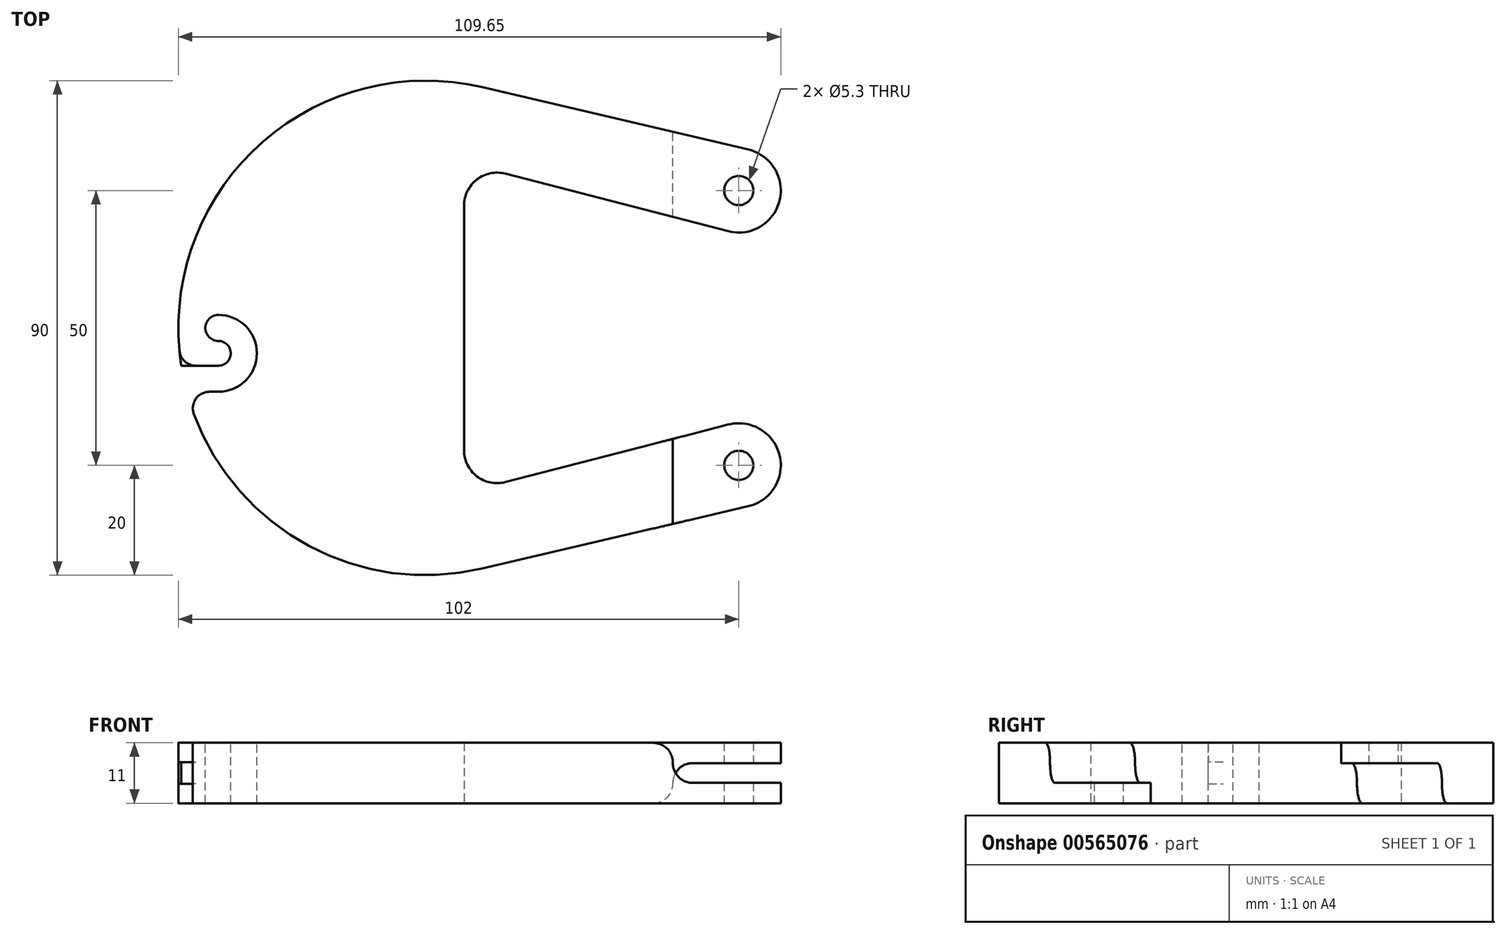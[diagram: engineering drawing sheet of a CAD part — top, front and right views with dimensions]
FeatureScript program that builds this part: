
annotation { "Feature Type Name" : "Feature", "Feature Type Description" : "" }
export const myFeature = defineFeature(function(context is Context, id is Id, definition is map)
    precondition{}
    {
        {
            var Q0;
            Q0=qCreatedBy(makeId("Top.planeOp"),FACE);
            var sketch = newSketch(context, id + "F0", { "sketchPlane" : qUnion([Q0])});
            skLineSegment(sketch, "E0", {"start": v(0, -25) * mm, "end": v(98, -25) * mm, "construction": true});
            skCircle(sketch, "E1", {"center": v(98, -25) * mm, "radius": 2.65 * mm});
            skLineSegment(sketch, "E2", {"start": v(0, 25) * mm, "end": v(98, 25) * mm, "construction": true});
            skLineSegment(sketch, "E3", {"start": v(0, 25) * mm, "end": v(0, 0) * mm, "construction": true});
            skLineSegment(sketch, "E4", {"start": v(0, 0) * mm, "end": v(0, -25) * mm, "construction": true});
            skCircle(sketch, "E5", {"center": v(98, 25) * mm, "radius": 2.65 * mm});
            skCircle(sketch, "E6.0", {"center": v(98, -25) * mm, "radius": 7.65 * mm});
            skLineSegment(sketch, "E7", {"start": v(51.27, -43.81) * mm, "end": v(99.75, -32.45) * mm});
            skCircle(sketch, "E8", {"center": v(98, 25) * mm, "radius": 7.65 * mm});
            skLineSegment(sketch, "E9", {"start": v(99.75, 32.45) * mm, "end": v(51.27, 43.81) * mm});
            skLineSegment(sketch, "E10", {"start": v(48, 22.26) * mm, "end": v(48, -22.26) * mm});
            skLineSegment(sketch, "E11", {"start": v(0, 0) * mm, "end": v(48, 0) * mm, "construction": true});
            skLineSegment(sketch, "E12", {"start": v(55.5, -28.07) * mm, "end": v(96.09, -17.6) * mm});
            skLineSegment(sketch, "E13", {"start": v(96.09, 17.6) * mm, "end": v(55.5, 28.07) * mm});
            skPoint(sketch, "E14.visualSharp", {"position": v(48, 30) * mm});
            skArc(sketch, "E14.filletArc", {"start": v(55.5, 28.07) * mm, "mid": v(50.33, 27) * mm, "end": v(48, 22.26) * mm});
            skPoint(sketch, "E15.visualSharp", {"position": v(48, -30) * mm});
            skArc(sketch, "E15.filletArc", {"start": v(48, -22.26) * mm, "mid": v(50.33, -27) * mm, "end": v(55.5, -28.07) * mm});
            skArc(sketch, "E16", {"start": v(51.27, 43.81) * mm, "mid": v(-4, 0) * mm, "end": v(51.27, -43.81) * mm});
            skSolve(sketch);
        }
        {
            var Q0;
            {var subQ3=sQuery(id+"F0.wireOp",EDGE,"E7");Q0=makeQuery(id+"F0.imprint","IMPRINT",FACE,{"disambiguationData":[TD([[makeQuery(id+"F0.imprint","IMPRINT",EDGE,{"derivedFrom":subQ3}),1.0]])]});}
            var Q1;
            Q1=makeQuery(id+"F0.imprint","IMPRINT",FACE,{"disambiguationData":[TD([[makeQuery(id+"F0.imprint","IMPRINT",EDGE,{"derivedFrom":sQuery(id+"F0.wireOp",EDGE,"E5")}),-1.0]])]});
            var Q2;
            Q2=makeQuery(id+"F0.imprint","IMPRINT",FACE,{"disambiguationData":[TD([[makeQuery(id+"F0.imprint","IMPRINT",EDGE,{"derivedFrom":sQuery(id+"F0.wireOp",EDGE,"E1")}),-1.0]])]});
            extrude(context, id + "F1", {"entities" : qUnion([Q0, Q1, Q2]), "depth" : 4 * mm, "offsetDistance" : 25 * mm});
        }
        {
            var Q0;
            Q0=makeQuery(id+"F1.opExtrude","CAP_FACE",FACE,{"disambiguationData":[OSD([sQuery(id+"F0.wireOp",EDGE,"xxKo6WRD-6QPB-TjOC-Ujmc-5RzxxUmcmt8J"),sQuery(id+"F0.wireOp",EDGE,"E1"),sQuery(id+"F0.wireOp",EDGE,"E5"),sQuery(id+"F0.wireOp",EDGE,"E6.0"),sQuery(id+"F0.wireOp",EDGE,"E7"),sQuery(id+"F0.wireOp",EDGE,"E8"),sQuery(id+"F0.wireOp",EDGE,"E9"),sQuery(id+"F0.wireOp",EDGE,"E10"),sQuery(id+"F0.wireOp",EDGE,"E12"),sQuery(id+"F0.wireOp",EDGE,"E13"),sQuery(id+"F0.wireOp",EDGE,"E14.filletArc"),sQuery(id+"F0.wireOp",EDGE,"E15.filletArc")])],"isStart":false});
            var sketch = newSketch(context, id + "F2", { "sketchPlane" : qUnion([Q0])});
            skArc(sketch, "E17", {"start": v(3.28, -11.63) * mm, "mid": v(10.28, -4.63) * mm, "end": v(3.28, 2.37) * mm});
            skPoint(sketch, "E17.centerSnap0", {"position": v(-4, 0) * mm});
            skArc(sketch, "E18", {"start": v(3.28, -6.88) * mm, "mid": v(5.53, -4.63) * mm, "end": v(3.28, -2.38) * mm});
            skArc(sketch, "E19", {"start": v(3.28, 2.37) * mm, "mid": v(0.9, 0) * mm, "end": v(3.28, -2.38) * mm});
            skLineSegment(sketch, "E20", {"start": v(3.28, -6.88) * mm, "end": v(-3.47, -6.88) * mm});
            skLineSegment(sketch, "E21", {"start": v(3.28, -11.63) * mm, "end": v(-2.47, -11.63) * mm});
            skLineSegment(sketch, "E22.0.0", {"start": v(99.75, -32.45) * mm, "end": v(51.27, -43.81) * mm});
            skArc(sketch, "E22.0.1", {"start": v(51.27, -43.81) * mm, "mid": v(-4, 0) * mm, "end": v(51.27, 43.81) * mm});
            skLineSegment(sketch, "E22.0.2", {"start": v(51.27, 43.81) * mm, "end": v(99.75, 32.45) * mm});
            skArc(sketch, "E22.0.3", {"start": v(99.75, 32.45) * mm, "mid": v(105.43, 23.17) * mm, "end": v(96.09, 17.6) * mm});
            skLineSegment(sketch, "E22.0.4", {"start": v(96.09, 17.6) * mm, "end": v(55.5, 28.07) * mm});
            skArc(sketch, "E22.0.5", {"start": v(55.5, 28.07) * mm, "mid": v(50.33, 27) * mm, "end": v(48, 22.26) * mm});
            skLineSegment(sketch, "E22.0.6", {"start": v(48, 22.26) * mm, "end": v(48, -22.26) * mm});
            skArc(sketch, "E22.0.7", {"start": v(48, -22.26) * mm, "mid": v(50.33, -27) * mm, "end": v(55.5, -28.07) * mm});
            skLineSegment(sketch, "E22.0.8", {"start": v(55.5, -28.07) * mm, "end": v(96.09, -17.6) * mm});
            skArc(sketch, "E22.0.9", {"start": v(96.09, -17.6) * mm, "mid": v(105.43, -23.17) * mm, "end": v(99.75, -32.45) * mm});
            skSolve(sketch);
        }
        {
            var Q0;
            Q0=makeQuery(id+"F2.imprint","IMPRINT",FACE,{"disambiguationData":[TD([[makeQuery(id+"F2.imprint","IMPRINT",EDGE,{"derivedFrom":sQuery(id+"F2.wireOp",EDGE,"E17")}),1.0]])]});
            extrude(context, id + "F3", {"entities" : qUnion([Q0]), "operationType" : NewBodyOperationType.REMOVE, "endBound" : BoundingType.THROUGH_ALL, "oppositeDirection" : true, "depth" : 25 * mm, "offsetDistance" : 25 * mm});
        }
        {
            var Q0;
            Q0=makeQuery(id+"F3.boolean.opBoolean","COPY",EDGE,{"derivedFrom":makeQuery(id+"F3.opExtrude","SWEPT_EDGE",EDGE,{"disambiguationData":[OSD([sQuery(id+"F0.wireOp",EDGE,"xxKo6WRD-6QPB-TjOC-Ujmc-5RzxxUmcmt8J"),sQuery(id+"F2.wireOp",EDGE,"E20")])]})});
            var Q1;
            Q1=makeQuery(id+"F3.boolean.opBoolean","COPY",EDGE,{"derivedFrom":makeQuery(id+"F3.opExtrude","SWEPT_EDGE",EDGE,{"disambiguationData":[OSD([sQuery(id+"F0.wireOp",EDGE,"xxKo6WRD-6QPB-TjOC-Ujmc-5RzxxUmcmt8J"),sQuery(id+"F2.wireOp",EDGE,"E21")])]})});
            fillet(context, id + "F4", {"entities" : qUnion([Q0, Q1]), "radius" : 3 * mm, "tangentPropagation" : true, "allowEdgeOverflow" : false});
        }
        {
            var Q0;
            Q0=makeQuery(id+"F1.opExtrude","CAP_FACE",FACE,{"disambiguationData":[OSD([sQuery(id+"F0.wireOp",EDGE,"xxKo6WRD-6QPB-TjOC-Ujmc-5RzxxUmcmt8J"),sQuery(id+"F0.wireOp",EDGE,"E1"),sQuery(id+"F0.wireOp",EDGE,"E5"),sQuery(id+"F0.wireOp",EDGE,"E6.0"),sQuery(id+"F0.wireOp",EDGE,"E7"),sQuery(id+"F0.wireOp",EDGE,"E8"),sQuery(id+"F0.wireOp",EDGE,"E9"),sQuery(id+"F0.wireOp",EDGE,"E10"),sQuery(id+"F0.wireOp",EDGE,"E12"),sQuery(id+"F0.wireOp",EDGE,"E13"),sQuery(id+"F0.wireOp",EDGE,"E14.filletArc"),sQuery(id+"F0.wireOp",EDGE,"E15.filletArc")])],"isStart":true});
            var sketch = newSketch(context, id + "F5", { "sketchPlane" : qUnion([Q0])});
            skArc(sketch, "E23.0.4", {"start": v(99.75, -32.45) * mm, "mid": v(105.43, -23.17) * mm, "end": v(96.09, -17.6) * mm});
            skLineSegment(sketch, "E23.0.5", {"start": v(96.09, -17.6) * mm, "end": v(55.5, -28.07) * mm});
            skArc(sketch, "E23.0.6", {"start": v(55.5, -28.07) * mm, "mid": v(50.33, -27) * mm, "end": v(48, -22.26) * mm});
            skLineSegment(sketch, "E23.0.7", {"start": v(48, -22.26) * mm, "end": v(48, 22.26) * mm});
            skLineSegment(sketch, "E23.0.9", {"start": v(55.5, 28.07) * mm, "end": v(96.09, 17.6) * mm});
            skArc(sketch, "E23.0.10", {"start": v(96.09, 17.6) * mm, "mid": v(105.43, 23.17) * mm, "end": v(99.75, 32.45) * mm});
            skLineSegment(sketch, "E23.0.11", {"start": v(99.75, 32.45) * mm, "end": v(51.27, 43.81) * mm});
            skCircle(sketch, "E24.0", {"center": v(98, 25) * mm, "radius": 2.65 * mm});
            skLineSegment(sketch, "E25", {"start": v(82, 36.6) * mm, "end": v(82, 21.23) * mm});
            skSolve(sketch);
        }
        {
            var Q0;
            {var subQ1=sQuery(id+"F5.wireOp",EDGE,"E23.0.10");Q0=makeQuery(id+"F5.imprint","IMPRINT",FACE,{"disambiguationData":[TD([[makeQuery(id+"F5.imprint","IMPRINT",EDGE,{"derivedFrom":subQ1}),-1.0]])]});}
            extrude(context, id + "F6", {"entities" : qUnion([Q0]), "operationType" : NewBodyOperationType.ADD, "depth" : 3.5 * mm, "offsetDistance" : 25 * mm});
        }
        {
            var Q0;
            Q0=makeQuery(id+"F1.opExtrude","CAP_FACE",FACE,{"disambiguationData":[OSD([sQuery(id+"F0.wireOp",EDGE,"xxKo6WRD-6QPB-TjOC-Ujmc-5RzxxUmcmt8J"),sQuery(id+"F0.wireOp",EDGE,"E1"),sQuery(id+"F0.wireOp",EDGE,"E5"),sQuery(id+"F0.wireOp",EDGE,"E6.0"),sQuery(id+"F0.wireOp",EDGE,"E7"),sQuery(id+"F0.wireOp",EDGE,"E8"),sQuery(id+"F0.wireOp",EDGE,"E9"),sQuery(id+"F0.wireOp",EDGE,"E10"),sQuery(id+"F0.wireOp",EDGE,"E12"),sQuery(id+"F0.wireOp",EDGE,"E13"),sQuery(id+"F0.wireOp",EDGE,"E14.filletArc"),sQuery(id+"F0.wireOp",EDGE,"E15.filletArc")])],"isStart":false});
            var sketch = newSketch(context, id + "F7", { "sketchPlane" : qUnion([Q0])});
            skLineSegment(sketch, "E26", {"start": v(86, -20.2) * mm, "end": v(86, -35.67) * mm});
            skArc(sketch, "E27.0.10", {"start": v(99.75, -32.45) * mm, "mid": v(105.43, -23.17) * mm, "end": v(96.09, -17.6) * mm});
            skLineSegment(sketch, "E27.0.11", {"start": v(96.09, -17.6) * mm, "end": v(55.5, -28.07) * mm});
            skArc(sketch, "E27.0.12", {"start": v(55.5, -28.07) * mm, "mid": v(50.33, -27) * mm, "end": v(48, -22.26) * mm});
            skLineSegment(sketch, "E27.0.13", {"start": v(48, -22.26) * mm, "end": v(48, 22.26) * mm});
            skArc(sketch, "E27.0.14", {"start": v(48, 22.26) * mm, "mid": v(50.33, 27) * mm, "end": v(55.5, 28.07) * mm});
            skLineSegment(sketch, "E27.0.15", {"start": v(55.5, 28.07) * mm, "end": v(96.09, 17.6) * mm});
            skArc(sketch, "E27.0.16", {"start": v(96.09, 17.6) * mm, "mid": v(105.43, 23.17) * mm, "end": v(99.75, 32.45) * mm});
            skCircle(sketch, "E28.0", {"center": v(98, -25) * mm, "radius": 2.65 * mm});
            skSolve(sketch);
        }
        {
            var Q0;
            {var subQ2=sQuery(id+"F7.wireOp",EDGE,"E26");Q0=makeQuery(id+"F7.imprint","IMPRINT",FACE,{"disambiguationData":[TD([[makeQuery(id+"F7.imprint","IMPRINT",EDGE,{"derivedFrom":subQ2}),1.0]])]});}
            extrude(context, id + "F8", {"entities" : qUnion([Q0]), "operationType" : NewBodyOperationType.REMOVE, "oppositeDirection" : true, "depth" : 3.8 * mm, "offsetDistance" : 25 * mm});
        }
        {
            var Q0;
            Q0=qCreatedBy(makeId("Front.planeOp"),FACE);
            var sketch = newSketch(context, id + "F9", { "sketchPlane" : qUnion([Q0])});
            skLineSegment(sketch, "E29.0", {"start": v(82, -3.5) * mm, "end": v(82, 0) * mm});
            skLineSegment(sketch, "E30.0", {"start": v(86, 0.2) * mm, "end": v(86, 4) * mm});
            skLineSegment(sketch, "E31.0", {"start": v(55.5, 0) * mm, "end": v(82, 0) * mm});
            skLineSegment(sketch, "E32.0", {"start": v(82, -3.5) * mm, "end": v(96.09, -3.5) * mm});
            skLineSegment(sketch, "E33", {"start": v(82, -3.5) * mm, "end": v(55.5, 0) * mm});
            skSolve(sketch);
        }
        {
            var Q0;
            Q0=makeQuery(id+"F1.opExtrude","CAP_FACE",FACE,{"disambiguationData":[OSD([sQuery(id+"F0.wireOp",EDGE,"xxKo6WRD-6QPB-TjOC-Ujmc-5RzxxUmcmt8J"),sQuery(id+"F0.wireOp",EDGE,"E1"),sQuery(id+"F0.wireOp",EDGE,"E5"),sQuery(id+"F0.wireOp",EDGE,"E6.0"),sQuery(id+"F0.wireOp",EDGE,"E7"),sQuery(id+"F0.wireOp",EDGE,"E8"),sQuery(id+"F0.wireOp",EDGE,"E9"),sQuery(id+"F0.wireOp",EDGE,"E10"),sQuery(id+"F0.wireOp",EDGE,"E12"),sQuery(id+"F0.wireOp",EDGE,"E13"),sQuery(id+"F0.wireOp",EDGE,"E14.filletArc"),sQuery(id+"F0.wireOp",EDGE,"E15.filletArc")])],"isStart":false});
            var sketch = newSketch(context, id + "F10", { "sketchPlane" : qUnion([Q0])});
            skArc(sketch, "E34.0.2", {"start": v(55.5, -28.07) * mm, "mid": v(50.33, -27) * mm, "end": v(48, -22.26) * mm});
            skLineSegment(sketch, "E34.0.3", {"start": v(48, -22.26) * mm, "end": v(48, 22.26) * mm});
            skArc(sketch, "E34.0.4", {"start": v(48, 22.26) * mm, "mid": v(50.33, 27) * mm, "end": v(55.5, 28.07) * mm});
            skLineSegment(sketch, "E34.0.5", {"start": v(55.5, 28.07) * mm, "end": v(96.09, 17.6) * mm});
            skArc(sketch, "E34.0.6", {"start": v(96.09, 17.6) * mm, "mid": v(105.43, 23.17) * mm, "end": v(99.75, 32.45) * mm});
            skLineSegment(sketch, "E34.0.7", {"start": v(99.75, 32.45) * mm, "end": v(99.75, 32.45) * mm});
            skLineSegment(sketch, "E34.0.14", {"start": v(3.28, -11.63) * mm, "end": v(1.63, -11.63) * mm});
            skCircle(sketch, "E35.0", {"center": v(98, 25) * mm, "radius": 2.65 * mm});
            skLineSegment(sketch, "E36", {"start": v(82, 21.23) * mm, "end": v(82, 36.6) * mm});
            skLineSegment(sketch, "E37.0.7", {"start": v(99.75, 32.45) * mm, "end": v(51.27, 43.81) * mm});
            skArc(sketch, "E37.0.16", {"start": v(-1.18, -15.67) * mm, "mid": v(19.73, -39.65) * mm, "end": v(51.27, -43.81) * mm});
            skArc(sketch, "E38.0.8", {"start": v(51.27, 43.81) * mm, "mid": v(11.45, 33.94) * mm, "end": v(-3.8, -4.15) * mm});
            skArc(sketch, "E38.0.9", {"start": v(-3.8, -4.15) * mm, "mid": v(-2.84, -6.1) * mm, "end": v(-0.82, -6.88) * mm});
            skLineSegment(sketch, "E38.0.10", {"start": v(-0.82, -6.88) * mm, "end": v(3.28, -6.88) * mm});
            skArc(sketch, "E38.0.11", {"start": v(3.28, -6.88) * mm, "mid": v(5.53, -4.63) * mm, "end": v(3.28, -2.38) * mm});
            skArc(sketch, "E38.0.12", {"start": v(3.28, -2.38) * mm, "mid": v(0.9, 0) * mm, "end": v(3.28, 2.37) * mm});
            skArc(sketch, "E38.0.13", {"start": v(3.28, 2.37) * mm, "mid": v(10.28, -4.63) * mm, "end": v(3.28, -11.63) * mm});
            skArc(sketch, "E38.0.15", {"start": v(1.63, -11.63) * mm, "mid": v(-0.83, -12.91) * mm, "end": v(-1.18, -15.67) * mm});
            skSolve(sketch);
        }
        {
            var Q0;
            Q0=makeQuery(id+"F10.imprint","IMPRINT",FACE,{"disambiguationData":[TD([[makeQuery(id+"F10.imprint","IMPRINT",EDGE,{"derivedFrom":sQuery(id+"F10.wireOp",EDGE,"E35.0")}),-1.0]])]});
            extrude(context, id + "F11", {"entities" : qUnion([Q0]), "operationType" : NewBodyOperationType.ADD, "depth" : 3.5 * mm, "offsetDistance" : 25 * mm});
        }
        {
            var Q0;
            Q0=makeQuery(id+"F1.opExtrude","CAP_FACE",FACE,{"disambiguationData":[OSD([sQuery(id+"F0.wireOp",EDGE,"xxKo6WRD-6QPB-TjOC-Ujmc-5RzxxUmcmt8J"),sQuery(id+"F0.wireOp",EDGE,"E1"),sQuery(id+"F0.wireOp",EDGE,"E5"),sQuery(id+"F0.wireOp",EDGE,"E6.0"),sQuery(id+"F0.wireOp",EDGE,"E7"),sQuery(id+"F0.wireOp",EDGE,"E8"),sQuery(id+"F0.wireOp",EDGE,"E9"),sQuery(id+"F0.wireOp",EDGE,"E10"),sQuery(id+"F0.wireOp",EDGE,"E12"),sQuery(id+"F0.wireOp",EDGE,"E13"),sQuery(id+"F0.wireOp",EDGE,"E14.filletArc"),sQuery(id+"F0.wireOp",EDGE,"E15.filletArc")])],"isStart":true});
            var sketch = newSketch(context, id + "F12", { "sketchPlane" : qUnion([Q0])});
            skLineSegment(sketch, "E39", {"start": v(86, -20.2) * mm, "end": v(86, -35.67) * mm});
            skLineSegment(sketch, "E40.0.0", {"start": v(55.5, 28.07) * mm, "end": v(55.5, 42.82) * mm});
            skLineSegment(sketch, "E40.0.1", {"start": v(55.5, 42.82) * mm, "end": v(51.27, 43.81) * mm});
            skArc(sketch, "E40.0.12", {"start": v(99.75, -32.45) * mm, "mid": v(105.43, -23.17) * mm, "end": v(96.09, -17.6) * mm});
            skLineSegment(sketch, "E40.0.13", {"start": v(96.09, -17.6) * mm, "end": v(55.5, -28.07) * mm});
            skArc(sketch, "E40.0.14", {"start": v(55.5, -28.07) * mm, "mid": v(50.33, -27) * mm, "end": v(48, -22.26) * mm});
            skLineSegment(sketch, "E40.0.15", {"start": v(48, -22.26) * mm, "end": v(48, 22.26) * mm});
            skArc(sketch, "E40.0.16", {"start": v(48, 22.26) * mm, "mid": v(50.33, 27) * mm, "end": v(55.5, 28.07) * mm});
            skCircle(sketch, "E41.0", {"center": v(98, -25) * mm, "radius": 2.65 * mm});
            skArc(sketch, "E42.0.2", {"start": v(51.27, 43.81) * mm, "mid": v(19.73, 39.65) * mm, "end": v(-1.18, 15.67) * mm});
            skArc(sketch, "E42.0.3", {"start": v(-1.18, 15.67) * mm, "mid": v(-0.83, 12.91) * mm, "end": v(1.63, 11.63) * mm});
            skLineSegment(sketch, "E42.0.4", {"start": v(1.63, 11.63) * mm, "end": v(3.28, 11.63) * mm});
            skArc(sketch, "E42.0.5", {"start": v(3.28, 11.63) * mm, "mid": v(10.28, 4.63) * mm, "end": v(3.28, -2.37) * mm});
            skArc(sketch, "E42.0.6", {"start": v(3.28, -2.37) * mm, "mid": v(0.9, 0) * mm, "end": v(3.28, 2.38) * mm});
            skArc(sketch, "E42.0.7", {"start": v(3.28, 2.38) * mm, "mid": v(5.53, 4.63) * mm, "end": v(3.28, 6.88) * mm});
            skLineSegment(sketch, "E42.0.8", {"start": v(3.28, 6.88) * mm, "end": v(-0.82, 6.88) * mm});
            skArc(sketch, "E42.0.9", {"start": v(-0.82, 6.88) * mm, "mid": v(-2.84, 6.1) * mm, "end": v(-3.8, 4.15) * mm});
            skArc(sketch, "E42.0.10", {"start": v(-3.8, 4.15) * mm, "mid": v(11.45, -33.94) * mm, "end": v(51.27, -43.81) * mm});
            skLineSegment(sketch, "E42.0.11", {"start": v(51.27, -43.81) * mm, "end": v(99.75, -32.45) * mm});
            skSolve(sketch);
        }
        {
            var Q0;
            {var subQ2=sQuery(id+"F12.wireOp",EDGE,"E39");Q0=makeQuery(id+"F12.imprint","IMPRINT",FACE,{"disambiguationData":[TD([[makeQuery(id+"F12.imprint","IMPRINT",EDGE,{"derivedFrom":subQ2}),1.0]])]});}
            extrude(context, id + "F13", {"entities" : qUnion([Q0]), "operationType" : NewBodyOperationType.REMOVE, "oppositeDirection" : true, "depth" : 3.8 * mm, "offsetDistance" : 25 * mm});
        }
        {
            var Q0;
            Q0=qCreatedBy(makeId("Front.planeOp"),FACE);
            var sketch = newSketch(context, id + "F14", { "sketchPlane" : qUnion([Q0])});
            skLineSegment(sketch, "E43.0", {"start": v(82, 4) * mm, "end": v(82, 7.5) * mm});
            skLineSegment(sketch, "E44.0", {"start": v(82, 4) * mm, "end": v(51.27, 4) * mm});
            skLineSegment(sketch, "E45.0", {"start": v(82, 4) * mm, "end": v(55.5, 4) * mm});
            skLineSegment(sketch, "E46", {"start": v(82, 7.5) * mm, "end": v(55.5, 4) * mm});
            skSolve(sketch);
        }
        {
            var Q0;
            Q0=makeQuery(id+"F1.opExtrude","CAP_FACE",FACE,{"disambiguationData":[OSD([sQuery(id+"F0.wireOp",EDGE,"E1"),sQuery(id+"F0.wireOp",EDGE,"E5"),sQuery(id+"F0.wireOp",EDGE,"E6.0"),sQuery(id+"F0.wireOp",EDGE,"E7"),sQuery(id+"F0.wireOp",EDGE,"E8"),sQuery(id+"F0.wireOp",EDGE,"E9"),sQuery(id+"F0.wireOp",EDGE,"E10"),sQuery(id+"F0.wireOp",EDGE,"E12"),sQuery(id+"F0.wireOp",EDGE,"E13"),sQuery(id+"F0.wireOp",EDGE,"E14.filletArc"),sQuery(id+"F0.wireOp",EDGE,"E15.filletArc"),sQuery(id+"F0.wireOp",EDGE,"E16")])],"isStart":false});
            var sketch = newSketch(context, id + "F15", { "sketchPlane" : qUnion([Q0])});
            skLineSegment(sketch, "E47.0.0", {"start": v(55.5, 28.07) * mm, "end": v(82, 21.23) * mm});
            skLineSegment(sketch, "E47.0.1", {"start": v(82, 21.23) * mm, "end": v(82, 36.6) * mm});
            skLineSegment(sketch, "E47.0.2", {"start": v(82, 36.6) * mm, "end": v(51.27, 43.81) * mm});
            skArc(sketch, "E47.0.3", {"start": v(51.27, 43.81) * mm, "mid": v(11.45, 33.94) * mm, "end": v(-3.8, -4.15) * mm});
            skArc(sketch, "E47.0.4", {"start": v(-3.8, -4.15) * mm, "mid": v(-2.84, -6.1) * mm, "end": v(-0.82, -6.88) * mm});
            skLineSegment(sketch, "E47.0.5", {"start": v(-0.82, -6.88) * mm, "end": v(3.28, -6.88) * mm});
            skArc(sketch, "E47.0.6", {"start": v(3.28, -6.88) * mm, "mid": v(5.53, -4.63) * mm, "end": v(3.28, -2.38) * mm});
            skArc(sketch, "E47.0.7", {"start": v(3.28, -2.38) * mm, "mid": v(0.9, 0) * mm, "end": v(3.28, 2.37) * mm});
            skArc(sketch, "E47.0.8", {"start": v(3.28, 2.37) * mm, "mid": v(10.28, -4.63) * mm, "end": v(3.28, -11.63) * mm});
            skLineSegment(sketch, "E47.0.9", {"start": v(3.28, -11.63) * mm, "end": v(1.63, -11.63) * mm});
            skArc(sketch, "E47.0.10", {"start": v(1.63, -11.63) * mm, "mid": v(-0.83, -12.91) * mm, "end": v(-1.18, -15.67) * mm});
            skArc(sketch, "E47.0.11", {"start": v(-1.18, -15.67) * mm, "mid": v(19.73, -39.65) * mm, "end": v(51.27, -43.81) * mm});
            skLineSegment(sketch, "E47.0.12", {"start": v(51.27, -43.81) * mm, "end": v(86, -35.67) * mm});
            skLineSegment(sketch, "E47.0.13", {"start": v(86, -35.67) * mm, "end": v(86, -20.2) * mm});
            skLineSegment(sketch, "E47.0.14", {"start": v(86, -20.2) * mm, "end": v(55.5, -28.07) * mm});
            skArc(sketch, "E47.0.15", {"start": v(55.5, -28.07) * mm, "mid": v(50.33, -27) * mm, "end": v(48, -22.26) * mm});
            skLineSegment(sketch, "E47.0.16", {"start": v(48, -22.26) * mm, "end": v(48, 22.26) * mm});
            skArc(sketch, "E47.0.17", {"start": v(48, 22.26) * mm, "mid": v(50.33, 27) * mm, "end": v(55.5, 28.07) * mm});
            skSolve(sketch);
        }
        {
            var Q0;
            Q0=makeQuery(id+"F15.imprint","IMPRINT",FACE,{"disambiguationData":[TD([[makeQuery(id+"F15.imprint","IMPRINT",EDGE,{"derivedFrom":sQuery(id+"F15.wireOp",EDGE,"E47.0.0")}),-1.0]])]});
            var Q1;
            Q1=makeQuery(id+"F11.opExtrude","CAP_FACE",FACE,{"disambiguationData":[OSD([sQuery(id+"F10.wireOp",EDGE,"E35.0"),sQuery(id+"F10.wireOp",EDGE,"E36"),sQuery(id+"F10.wireOp",EDGE,"E34.0.5"),sQuery(id+"F10.wireOp",EDGE,"E34.0.6"),sQuery(id+"F10.wireOp",EDGE,"E37.0.7")])],"isStart":false});
            extrude(context, id + "F16", {"entities" : qUnion([Q0]), "operationType" : NewBodyOperationType.ADD, "endBound" : BoundingType.UP_TO_SURFACE, "depth" : 25 * mm, "endBoundEntityFace" : qUnion([Q1]), "offsetDistance" : 25 * mm});
        }
        {
            var Q0;
            Q0=makeQuery(id+"F1.opExtrude","CAP_FACE",FACE,{"disambiguationData":[OSD([sQuery(id+"F0.wireOp",EDGE,"E1"),sQuery(id+"F0.wireOp",EDGE,"E5"),sQuery(id+"F0.wireOp",EDGE,"E6.0"),sQuery(id+"F0.wireOp",EDGE,"E7"),sQuery(id+"F0.wireOp",EDGE,"E8"),sQuery(id+"F0.wireOp",EDGE,"E9"),sQuery(id+"F0.wireOp",EDGE,"E10"),sQuery(id+"F0.wireOp",EDGE,"E12"),sQuery(id+"F0.wireOp",EDGE,"E13"),sQuery(id+"F0.wireOp",EDGE,"E14.filletArc"),sQuery(id+"F0.wireOp",EDGE,"E15.filletArc"),sQuery(id+"F0.wireOp",EDGE,"E16")])],"isStart":true});
            var sketch = newSketch(context, id + "F17", { "sketchPlane" : qUnion([Q0])});
            skLineSegment(sketch, "E48.0.0", {"start": v(86, -35.67) * mm, "end": v(86, -20.2) * mm});
            skLineSegment(sketch, "E48.0.1", {"start": v(86, -20.2) * mm, "end": v(55.5, -28.07) * mm});
            skArc(sketch, "E48.0.2", {"start": v(55.5, -28.07) * mm, "mid": v(50.33, -27) * mm, "end": v(48, -22.26) * mm});
            skLineSegment(sketch, "E48.0.3", {"start": v(48, -22.26) * mm, "end": v(48, 22.26) * mm});
            skArc(sketch, "E48.0.4", {"start": v(48, 22.26) * mm, "mid": v(50.33, 27) * mm, "end": v(55.5, 28.07) * mm});
            skLineSegment(sketch, "E48.0.5", {"start": v(55.5, 28.07) * mm, "end": v(82, 21.23) * mm});
            skLineSegment(sketch, "E48.0.6", {"start": v(82, 21.23) * mm, "end": v(82, 36.6) * mm});
            skLineSegment(sketch, "E48.0.7", {"start": v(82, 36.6) * mm, "end": v(51.27, 43.81) * mm});
            skArc(sketch, "E48.0.8", {"start": v(51.27, 43.81) * mm, "mid": v(19.73, 39.65) * mm, "end": v(-1.18, 15.67) * mm});
            skArc(sketch, "E48.0.9", {"start": v(-1.18, 15.67) * mm, "mid": v(-0.83, 12.91) * mm, "end": v(1.63, 11.63) * mm});
            skLineSegment(sketch, "E48.0.10", {"start": v(1.63, 11.63) * mm, "end": v(3.28, 11.63) * mm});
            skArc(sketch, "E48.0.11", {"start": v(3.28, 11.63) * mm, "mid": v(10.28, 4.63) * mm, "end": v(3.28, -2.37) * mm});
            skArc(sketch, "E48.0.12", {"start": v(3.28, -2.37) * mm, "mid": v(0.9, 0) * mm, "end": v(3.28, 2.38) * mm});
            skArc(sketch, "E48.0.13", {"start": v(3.28, 2.38) * mm, "mid": v(5.53, 4.63) * mm, "end": v(3.28, 6.88) * mm});
            skLineSegment(sketch, "E48.0.14", {"start": v(3.28, 6.88) * mm, "end": v(-0.82, 6.88) * mm});
            skArc(sketch, "E48.0.15", {"start": v(-0.82, 6.88) * mm, "mid": v(-2.84, 6.1) * mm, "end": v(-3.8, 4.15) * mm});
            skArc(sketch, "E48.0.16", {"start": v(-3.8, 4.15) * mm, "mid": v(11.45, -33.94) * mm, "end": v(51.27, -43.81) * mm});
            skLineSegment(sketch, "E48.0.17", {"start": v(51.27, -43.81) * mm, "end": v(86, -35.67) * mm});
            skSolve(sketch);
        }
        {
            var Q0;
            Q0=makeQuery(id+"F17.imprint","IMPRINT",FACE,{"disambiguationData":[TD([[makeQuery(id+"F17.imprint","IMPRINT",EDGE,{"derivedFrom":sQuery(id+"F17.wireOp",EDGE,"E48.0.0")}),-1.0]])]});
            var Q1;
            Q1=makeQuery(id+"F6.opExtrude","CAP_FACE",FACE,{"disambiguationData":[OSD([sQuery(id+"F5.wireOp",EDGE,"E23.0.9"),sQuery(id+"F5.wireOp",EDGE,"E23.0.10"),sQuery(id+"F5.wireOp",EDGE,"E23.0.11"),sQuery(id+"F5.wireOp",EDGE,"E24.0"),sQuery(id+"F5.wireOp",EDGE,"E25")])],"isStart":false});
            extrude(context, id + "F18", {"entities" : qUnion([Q0]), "operationType" : NewBodyOperationType.ADD, "endBound" : BoundingType.UP_TO_SURFACE, "depth" : 25 * mm, "endBoundEntityFace" : qUnion([Q1]), "offsetDistance" : 25 * mm});
        }
        {
            var Q0;
            Q0=makeQuery(id+"F16.opExtrude","CAP_EDGE",EDGE,{"disambiguationData":[OSD([sQuery(id+"F15.wireOp",EDGE,"E47.0.13")])],"isStart":false});
            var Q1;
            Q1=makeQuery(id+"F18.opExtrude","CAP_EDGE",EDGE,{"disambiguationData":[OSD([sQuery(id+"F17.wireOp",EDGE,"E48.0.0")])],"isStart":false});
            var Q2;
            Q2=makeQuery(id+"F8.boolean.opBoolean","COPY",EDGE,{"derivedFrom":makeQuery(id+"F8.opExtrude","CAP_EDGE",EDGE,{"disambiguationData":[OSD([sQuery(id+"F7.wireOp",EDGE,"E26")])],"isStart":false})});
            var Q3;
            Q3=makeQuery(id+"F13.boolean.opBoolean","COPY",EDGE,{"derivedFrom":makeQuery(id+"F13.opExtrude","CAP_EDGE",EDGE,{"disambiguationData":[OSD([sQuery(id+"F12.wireOp",EDGE,"E39")])],"isStart":false})});
            fillet(context, id + "F19", {"entities" : qUnion([Q0, Q1, Q2, Q3]), "radius" : 3.6 * mm, "tangentPropagation" : true, "allowEdgeOverflow" : false});
        }
    });
